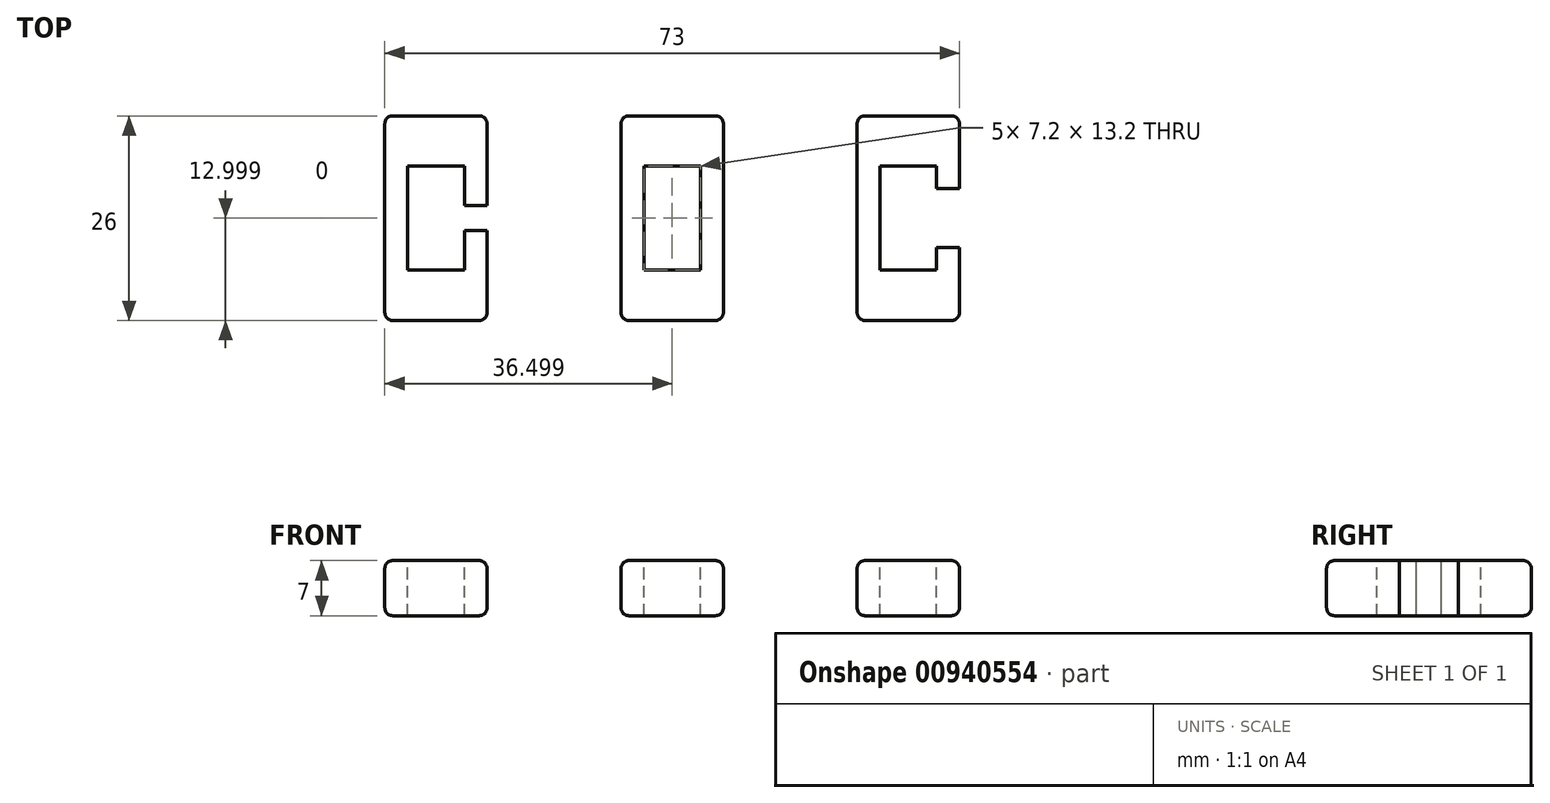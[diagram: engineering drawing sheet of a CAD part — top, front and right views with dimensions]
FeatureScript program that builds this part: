
annotation { "Feature Type Name" : "Feature", "Feature Type Description" : "" }
export const myFeature = defineFeature(function(context is Context, id is Id, definition is map)
    precondition{}
    {
        {
            var Q0;
            Q0=qCreatedBy(makeId("Top.planeOp"),FACE);
            var sketch = newSketch(context, id + "F0", { "sketchPlane" : qUnion([Q0])});
            skLineSegment(sketch, "E0.bottom", {"start": v(-6.78, 12.73) * mm, "end": v(6.22, 12.73) * mm});
            skLineSegment(sketch, "E0.top", {"start": v(-6.78, -13.27) * mm, "end": v(6.22, -13.27) * mm});
            skLineSegment(sketch, "E0.left", {"start": v(-6.78, 12.73) * mm, "end": v(-6.78, -13.27) * mm});
            skLineSegment(sketch, "E0.right", {"start": v(6.22, 12.73) * mm, "end": v(6.22, -13.27) * mm});
            skSolve(sketch);
        }
        {
            var Q0;
            Q0=makeQuery(id+"F0.imprint","IMPRINT",FACE,{"disambiguationData":[TD([[makeQuery(id+"F0.imprint","IMPRINT",EDGE,{"derivedFrom":sQuery(id+"F0.wireOp",EDGE,"E0.bottom")}),-1.0]])]});
            extrude(context, id + "F1", {"entities" : qUnion([Q0]), "depth" : -7 * mm, "offsetDistance" : 25 * mm});
        }
        {
            var Q0;
            Q0=makeQuery(id+"F1.opExtrude","CAP_FACE",FACE,{"disambiguationData":[OSD([sQuery(id+"F0.wireOp",EDGE,"E0.bottom"),sQuery(id+"F0.wireOp",EDGE,"E0.top"),sQuery(id+"F0.wireOp",EDGE,"E0.left"),sQuery(id+"F0.wireOp",EDGE,"E0.right")])],"isStart":true});
            var sketch = newSketch(context, id + "F2", { "sketchPlane" : qUnion([Q0])});
            skLineSegment(sketch, "E1.bottom", {"start": v(-3.88, 6.33) * mm, "end": v(3.32, 6.33) * mm});
            skLineSegment(sketch, "E1.top", {"start": v(-3.88, -6.87) * mm, "end": v(3.32, -6.87) * mm});
            skLineSegment(sketch, "E1.left", {"start": v(-3.88, 6.33) * mm, "end": v(-3.88, -6.87) * mm});
            skLineSegment(sketch, "E1.right", {"start": v(3.32, 6.33) * mm, "end": v(3.32, -6.87) * mm});
            skPoint(sketch, "E2", {"position": v(3.32, -0.27) * mm});
            skPoint(sketch, "E3", {"position": v(-0.28, 6.33) * mm});
            skPoint(sketch, "E4", {"position": v(-3.88, -0.27) * mm});
            skPoint(sketch, "E5", {"position": v(-0.28, -6.87) * mm});
            skPoint(sketch, "E6", {"position": v(-6.78, -0.27) * mm});
            skPoint(sketch, "E7", {"position": v(-0.28, 12.73) * mm});
            skPoint(sketch, "E8", {"position": v(6.22, -0.27) * mm});
            skPoint(sketch, "E9", {"position": v(-0.28, -13.27) * mm});
            skLineSegment(sketch, "E10", {"start": v(-0.28, 6.33) * mm, "end": v(-0.28, 12.73) * mm});
            skLineSegment(sketch, "E11", {"start": v(3.32, -0.27) * mm, "end": v(6.22, -0.27) * mm});
            skLineSegment(sketch, "E12", {"start": v(-3.88, -0.27) * mm, "end": v(-6.78, -0.27) * mm});
            skLineSegment(sketch, "E13", {"start": v(-0.28, -6.87) * mm, "end": v(-0.28, -13.27) * mm});
            skSolve(sketch);
        }
        {
            var Q0;
            Q0=makeQuery(id+"F2.imprint","IMPRINT",FACE,{"disambiguationData":[TD([[makeQuery(id+"F2.imprint","IMPRINT",EDGE,{"derivedFrom":sQuery(id+"F2.wireOp",EDGE,"E1.bottom")}),-1.0]])]});
            extrude(context, id + "F3", {"entities" : qUnion([Q0]), "operationType" : NewBodyOperationType.REMOVE, "endBound" : BoundingType.THROUGH_ALL, "oppositeDirection" : true, "depth" : -10 * mm, "offsetDistance" : 25 * mm});
        }
        {
            var Q0;
            Q0=makeQuery(id+"F1.opExtrude","SWEPT_EDGE",EDGE,{"disambiguationData":[OSD([sQuery(id+"F0.wireOp",EDGE,"E0.top"),sQuery(id+"F0.wireOp",EDGE,"E0.right")])]});
            var Q1;
            Q1=makeQuery(id+"F1.opExtrude","SWEPT_EDGE",EDGE,{"disambiguationData":[OSD([sQuery(id+"F0.wireOp",EDGE,"E0.bottom"),sQuery(id+"F0.wireOp",EDGE,"E0.right")])]});
            var Q2;
            Q2=makeQuery(id+"F1.opExtrude","SWEPT_EDGE",EDGE,{"disambiguationData":[OSD([sQuery(id+"F0.wireOp",EDGE,"E0.top"),sQuery(id+"F0.wireOp",EDGE,"E0.left")])]});
            var Q3;
            Q3=makeQuery(id+"F1.opExtrude","SWEPT_EDGE",EDGE,{"disambiguationData":[OSD([sQuery(id+"F0.wireOp",EDGE,"E0.bottom"),sQuery(id+"F0.wireOp",EDGE,"E0.left")])]});
            var Q4;
            Q4=makeQuery(id+"F1.opExtrude","CAP_EDGE",EDGE,{"disambiguationData":[OSD([sQuery(id+"F0.wireOp",EDGE,"E0.right")])],"isStart":true});
            var Q5;
            Q5=makeQuery(id+"F1.opExtrude","CAP_EDGE",EDGE,{"disambiguationData":[OSD([sQuery(id+"F0.wireOp",EDGE,"E0.top")])],"isStart":true});
            var Q6;
            Q6=makeQuery(id+"F1.opExtrude","CAP_EDGE",EDGE,{"disambiguationData":[OSD([sQuery(id+"F0.wireOp",EDGE,"E0.left")])],"isStart":true});
            var Q7;
            Q7=makeQuery(id+"F1.opExtrude","CAP_EDGE",EDGE,{"disambiguationData":[OSD([sQuery(id+"F0.wireOp",EDGE,"E0.bottom")])],"isStart":true});
            var Q8;
            Q8=makeQuery(id+"F1.opExtrude","CAP_EDGE",EDGE,{"disambiguationData":[OSD([sQuery(id+"F0.wireOp",EDGE,"E0.top")])],"isStart":false});
            var Q9;
            Q9=makeQuery(id+"F1.opExtrude","CAP_EDGE",EDGE,{"disambiguationData":[OSD([sQuery(id+"F0.wireOp",EDGE,"E0.right")])],"isStart":false});
            var Q10;
            Q10=makeQuery(id+"F1.opExtrude","CAP_EDGE",EDGE,{"disambiguationData":[OSD([sQuery(id+"F0.wireOp",EDGE,"E0.bottom")])],"isStart":false});
            var Q11;
            Q11=makeQuery(id+"F1.opExtrude","CAP_EDGE",EDGE,{"disambiguationData":[OSD([sQuery(id+"F0.wireOp",EDGE,"E0.left")])],"isStart":false});
            fillet(context, id + "F4", {"entities" : qUnion([Q0, Q1, Q2, Q3, Q4, Q5, Q6, Q7, Q8, Q9, Q10, Q11]), "radius" : 1 * mm, "tangentPropagation" : true, "allowEdgeOverflow" : false});
        }
        {
            var Q0;
            Q0=makeQuery(id+"F1.opExtrude","SWEPT_BODY",BODY,{"disambiguationData":[OSD([sQuery(id+"F0.wireOp",EDGE,"E0.bottom"),sQuery(id+"F0.wireOp",EDGE,"E0.top"),sQuery(id+"F0.wireOp",EDGE,"E0.left"),sQuery(id+"F0.wireOp",EDGE,"E0.right")])]});
            transform(context, id + "F5", {"entities" : qUnion([Q0]), "transformType" : TransformType.TRANSLATION_3D, "dx" : 30 * mm, "dy" : 0 * mm, "dz" : 0 * mm, "makeCopy" : true});
        }
        {
            var Q0;
            Q0=makeQuery(id+"F5.opPattern","COPY",FACE,{"derivedFrom":makeQuery(id+"F1.opExtrude","CAP_FACE",FACE,{"disambiguationData":[OSD([sQuery(id+"F0.wireOp",EDGE,"E0.bottom"),sQuery(id+"F0.wireOp",EDGE,"E0.top"),sQuery(id+"F0.wireOp",EDGE,"E0.left"),sQuery(id+"F0.wireOp",EDGE,"E0.right")])],"isStart":true}),"instanceName":"1"});
            var sketch = newSketch(context, id + "F6", { "sketchPlane" : qUnion([Q0])});
            skLineSegment(sketch, "E14.bottom", {"start": v(30.12, 3.48) * mm, "end": v(40.12, 3.48) * mm});
            skLineSegment(sketch, "E14.top", {"start": v(30.12, -4.02) * mm, "end": v(40.12, -4.02) * mm});
            skLineSegment(sketch, "E14.left", {"start": v(30.12, 3.48) * mm, "end": v(30.12, -4.02) * mm});
            skLineSegment(sketch, "E14.right", {"start": v(40.12, 3.48) * mm, "end": v(40.12, -4.02) * mm});
            skPoint(sketch, "E15", {"position": v(30.12, -0.27) * mm});
            skPoint(sketch, "E16", {"position": v(26.12, -0.27) * mm});
            skSolve(sketch);
        }
        {
            var Q0;
            Q0 = qSketchRegion(id + "F6", true);
            extrude(context, id + "F7", {"entities" : qUnion([Q0]), "operationType" : NewBodyOperationType.REMOVE, "endBound" : BoundingType.THROUGH_ALL, "oppositeDirection" : true, "depth" : 25 * mm, "offsetDistance" : 25 * mm});
        }
        {
            var Q0;
            Q0=makeQuery(id+"F1.opExtrude","SWEPT_BODY",BODY,{"disambiguationData":[OSD([sQuery(id+"F0.wireOp",EDGE,"E0.bottom"),sQuery(id+"F0.wireOp",EDGE,"E0.top"),sQuery(id+"F0.wireOp",EDGE,"E0.left"),sQuery(id+"F0.wireOp",EDGE,"E0.right")])]});
            transform(context, id + "F8", {"entities" : qUnion([Q0]), "transformType" : TransformType.TRANSLATION_3D, "dx" : -30 * mm, "dy" : 0 * mm, "dz" : 0 * mm, "makeCopy" : true});
        }
        {
            var Q0;
            Q0=makeQuery(id+"F8.opPattern","COPY",FACE,{"derivedFrom":makeQuery(id+"F1.opExtrude","CAP_FACE",FACE,{"disambiguationData":[OSD([sQuery(id+"F0.wireOp",EDGE,"E0.bottom"),sQuery(id+"F0.wireOp",EDGE,"E0.top"),sQuery(id+"F0.wireOp",EDGE,"E0.left"),sQuery(id+"F0.wireOp",EDGE,"E0.right")])],"isStart":true}),"instanceName":"1"});
            var sketch = newSketch(context, id + "F9", { "sketchPlane" : qUnion([Q0])});
            skLineSegment(sketch, "E17.bottom", {"start": v(-29.88, 1.33) * mm, "end": v(-19.88, 1.33) * mm});
            skLineSegment(sketch, "E17.top", {"start": v(-29.88, -1.87) * mm, "end": v(-19.88, -1.87) * mm});
            skLineSegment(sketch, "E17.left", {"start": v(-29.88, 1.33) * mm, "end": v(-29.88, -1.87) * mm});
            skLineSegment(sketch, "E17.right", {"start": v(-19.88, 1.33) * mm, "end": v(-19.88, -1.87) * mm});
            skPoint(sketch, "E18", {"position": v(-29.88, -0.27) * mm});
            skSolve(sketch);
        }
        {
            var Q0;
            Q0 = qSketchRegion(id + "F9", true);
            extrude(context, id + "F10", {"entities" : qUnion([Q0]), "operationType" : NewBodyOperationType.REMOVE, "endBound" : BoundingType.THROUGH_ALL, "oppositeDirection" : true, "depth" : 25 * mm, "offsetDistance" : 25 * mm});
        }
    });
